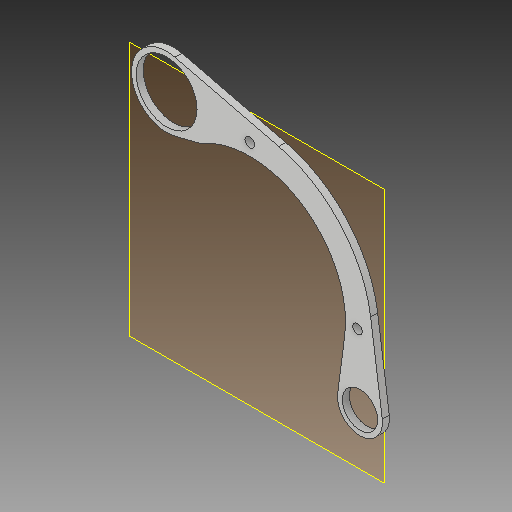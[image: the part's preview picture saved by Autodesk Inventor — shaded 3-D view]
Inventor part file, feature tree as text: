
AUTODESK INVENTOR PART (.ipt)
format: ipt  version: 2019.3 (Build 233278000, 278)  size: 136,704 bytes
history: native  units: in
note: dims shown in document units (in); Inventor stores cm internally (conversion verified against a paired STEP export)
features: reference x6, other x4, plane x1, extrude x1, sketch x1
ambient origin geometry x8: Origin, YZ Plane, XZ Plane, XY Plane, X Axis, Y Axis, Z Axis, Center Point
bodies: Solid1 (feature_tree)
feature tree (13):
  plane  "Work Plane1"
  extrude  "Extrusion1"  Depth=0.1575in
  sketch  "Sketch1"  dims[d1=0.1181in d2=1.5in d4=0.1181in d5=0.1575in d9=0.1732in d10=0.0in d16=0.1575in d17=4.7244in]
  reference  "Reference1"
  reference  "Reference2"
  reference  "Reference3"
  reference  "Reference4"
  reference  "Reference5"
  reference  "Reference6"
  other  "<userpath>\Desktop\3dprojects\OpenEmoto\Swingarm3\Swingarm3.iam"
  other  "Swingarm3.iam"
  other  "Denzel4500Motor:1"
  other  "Swingarm3:1"
